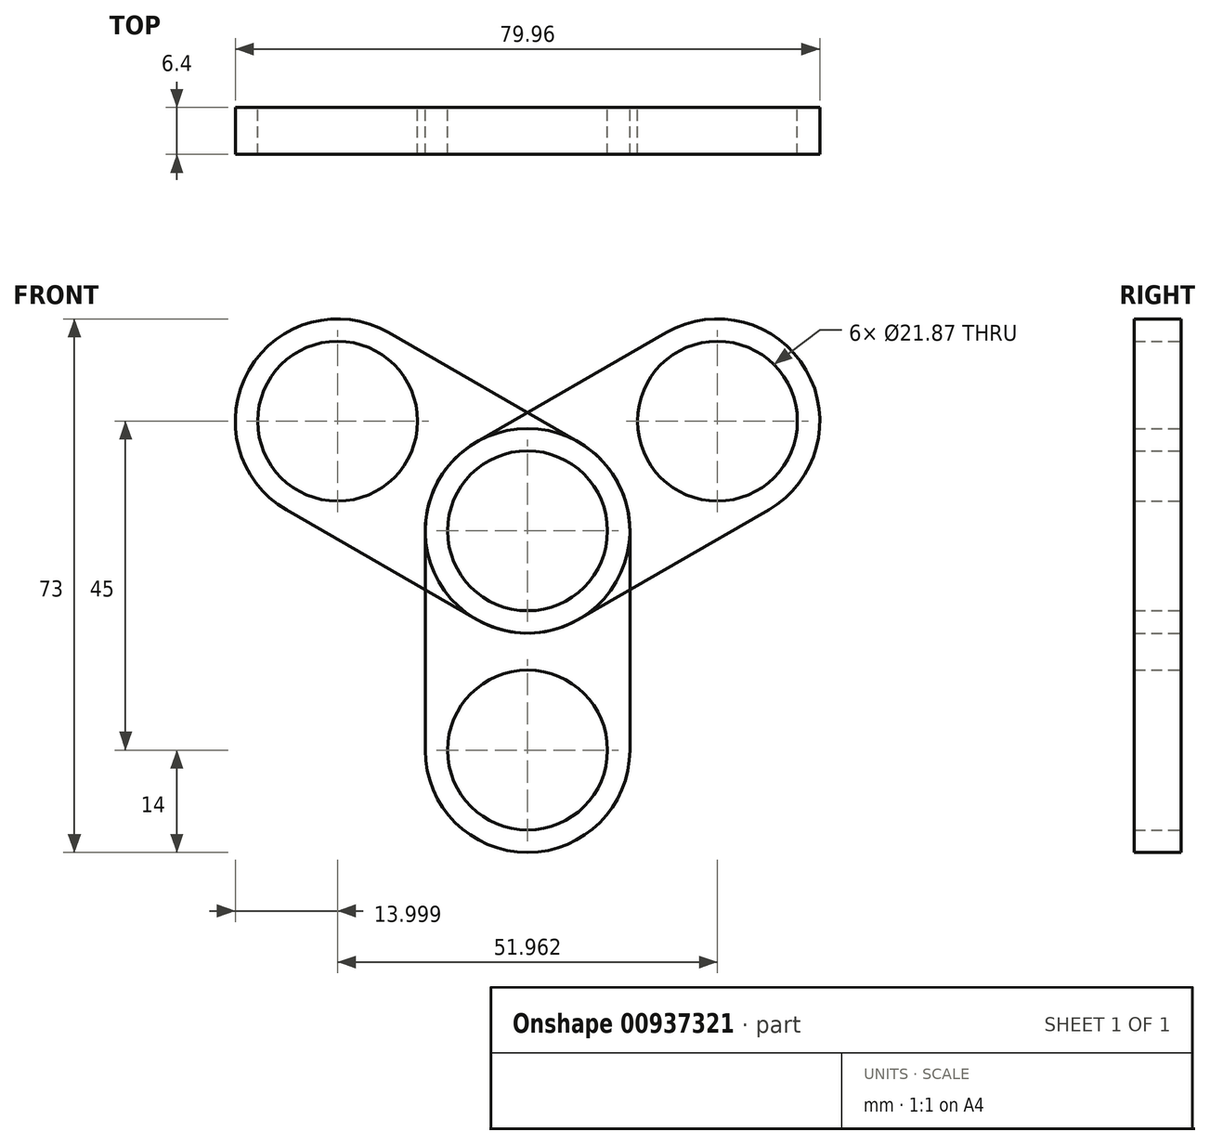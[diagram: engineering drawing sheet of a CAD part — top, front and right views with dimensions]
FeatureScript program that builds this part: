
annotation { "Feature Type Name" : "Feature", "Feature Type Description" : "" }
export const myFeature = defineFeature(function(context is Context, id is Id, definition is map)
    precondition{}
    {
        {
            var Q0;
            Q0=qCreatedBy(makeId("Front.planeOp"),FACE);
            var sketch = newSketch(context, id + "F0", { "sketchPlane" : qUnion([Q0])});
            skLineSegment(sketch, "E0.bottom", {"start": v(14, -15) * mm, "end": v(-14, -15) * mm});
            skLineSegment(sketch, "E0.top", {"start": v(14, 15) * mm, "end": v(-14, 15) * mm});
            skLineSegment(sketch, "E0.left", {"start": v(14, -15) * mm, "end": v(14, 15) * mm});
            skLineSegment(sketch, "E0.right", {"start": v(-14, -15) * mm, "end": v(-14, 15) * mm});
            skPoint(sketch, "E0.middle", {"position": v(0, 0) * mm});
            skCircle(sketch, "E1", {"center": v(0, 15) * mm, "radius": 14 * mm});
            skCircle(sketch, "E2", {"center": v(0, 15) * mm, "radius": 10.93 * mm});
            skCircle(sketch, "E3", {"center": v(0, -15) * mm, "radius": 14 * mm});
            skCircle(sketch, "E4", {"center": v(0, -15) * mm, "radius": 10.93 * mm});
            skSolve(sketch);
        }
        {
            var Q0;
            {var subQ1=sQuery(id+"F0.wireOp",EDGE,"E0.bottom");var subQ3=sQuery(id+"F0.wireOp",EDGE,"E4");var subQ4=makeQuery(id+"F0.imprint","INTERSECT",VERTEX,{"disambiguationData":[OD(0.0)],"derivedFrom":[subQ1,subQ3]});Q0=makeQuery(id+"F0.imprint","IMPRINT",FACE,{"disambiguationData":[TD([[makeQuery(id+"F0.imprint","IMPRINT",EDGE,{"disambiguationData":[TD([[subQ4,-1.0]])],"derivedFrom":subQ3}),-1.0]])]});}
            var Q1;
            {var subQ1=sQuery(id+"F0.wireOp",EDGE,"E0.bottom");var subQ3=sQuery(id+"F0.wireOp",EDGE,"E4");var subQ4=makeQuery(id+"F0.imprint","INTERSECT",VERTEX,{"disambiguationData":[OD(0.0)],"derivedFrom":[subQ1,subQ3]});Q1=makeQuery(id+"F0.imprint","IMPRINT",FACE,{"disambiguationData":[TD([[makeQuery(id+"F0.imprint","IMPRINT",EDGE,{"disambiguationData":[TD([[subQ4,1.0]])],"derivedFrom":subQ3}),-1.0]])]});}
            var Q2;
            {var subQ0=sQuery(id+"F0.wireOp",EDGE,"E0.left");Q2=makeQuery(id+"F0.imprint","IMPRINT",FACE,{"disambiguationData":[TD([[makeQuery(id+"F0.imprint","IMPRINT",EDGE,{"derivedFrom":subQ0}),1.0]])]});}
            var Q3;
            {var subQ1=sQuery(id+"F0.wireOp",EDGE,"E0.top");var subQ3=sQuery(id+"F0.wireOp",EDGE,"E2");var subQ4=makeQuery(id+"F0.imprint","INTERSECT",VERTEX,{"disambiguationData":[OD(0.0)],"derivedFrom":[subQ1,subQ3]});Q3=makeQuery(id+"F0.imprint","IMPRINT",FACE,{"disambiguationData":[TD([[makeQuery(id+"F0.imprint","IMPRINT",EDGE,{"disambiguationData":[TD([[subQ4,1.0]])],"derivedFrom":subQ3}),-1.0]])]});}
            var Q4;
            {var subQ1=sQuery(id+"F0.wireOp",EDGE,"E0.top");var subQ3=sQuery(id+"F0.wireOp",EDGE,"E2");var subQ4=makeQuery(id+"F0.imprint","INTERSECT",VERTEX,{"disambiguationData":[OD(0.0)],"derivedFrom":[subQ1,subQ3]});Q4=makeQuery(id+"F0.imprint","IMPRINT",FACE,{"disambiguationData":[TD([[makeQuery(id+"F0.imprint","IMPRINT",EDGE,{"disambiguationData":[TD([[subQ4,-1.0]])],"derivedFrom":subQ3}),-1.0]])]});}
            extrude(context, id + "F1", {"entities" : qUnion([Q0, Q1, Q2, Q3, Q4]), "depth" : 6.4 * mm, "offsetDistance" : 25.4 * mm});
        }
        {
            var Q0;
            Q0=makeQuery(id+"F1.opExtrude","SWEPT_BODY",BODY,{"disambiguationData":[OSD([sQuery(id+"F0.wireOp",EDGE,"E0.left"),sQuery(id+"F0.wireOp",EDGE,"E0.right"),sQuery(id+"F0.wireOp",EDGE,"E1"),sQuery(id+"F0.wireOp",EDGE,"E2"),sQuery(id+"F0.wireOp",EDGE,"E3"),sQuery(id+"F0.wireOp",EDGE,"E4")])]});
            var Q1;
            Q1=makeQuery(id+"F1.opExtrude","SWEPT_FACE",FACE,{"disambiguationData":[OSD([sQuery(id+"F0.wireOp",EDGE,"E1")])]});
            circularPattern(context, id + "F2", {"entities" : qUnion([Q0]), "axis" : qUnion([Q1]), "angle" : 360 * degree, "instanceCount" : 3, "equalSpace" : true});
        }
    });
